# Revit family: ROSENBERG_KHAS
name_source: partatom
category: Wyposażenie mechaniczne
revit_build: Autodesk Revit 2017 (Build: 20160225_1515(x64)
units: mm (PartAtom-declared; Revit-internal decimal feet)

## family parameters
Numer OmniClass = 23.75.00.00
Oparty na płaszczyźnie roboczej = Nie
Punkt obliczania pomieszczeń = Nie
Tnij formami wycięć po wczytaniu = Nie
Typ części = Dzieli na
Tytuł OmniClass = Climate Control (HVAC)
Współdzielony = Tak
Wymiar okrągłego złącza = Użyj średnicy
Zawsze pionowo = Tak

## types (13) — shared parameters
2R = 250 mm  [stored 0.82021 ft]
Axis_fan = 40 mm  [stored 0.131234 ft]
Date = 10.2018
Frequency = 50 Hz
Insulation = 20 mm  [stored 0.0656168 ft]
Maintenance_space = Tak
Material = <Wg kategorii>
Opis = Duct Fan
Producent = Rosenberg
R = 320 mm  [stored 1.04987 ft]
URL = https://www.rosenberg.pl
Version = 1

## per-type parameters (varying)
| type | Air_flow | Current | Fan | Height | Height_connector | Hole | Length | Model | Power | Pressure | Protection Class | Voltage | Weight | Width | Width_connector |
| 500-4.6HF WS_400V | 5260.0 m³/h | 3 A | 554 mm | 500 mm  [stored 1.64042 ft] | 500 mm  [stored 1.64042 ft] | 800 mm  [stored 2.62467 ft] | 880 mm | 500-4.6HF WS | 1770 W | 540.0 Pa | IP54 | 400 V | 88.00 kg | 800 mm  [stored 2.62467 ft] | 800 mm  [stored 2.62467 ft] |
| 500-4.6HF WS | 4238.0 m³/h | 7 A | 554 mm | 500 mm  [stored 1.64042 ft] | 500 mm  [stored 1.64042 ft] | 170 mm  [stored 0.557743 ft] | 880 mm | 500-4.6HF WS | 1650 W | 540.0 Pa | IP54 | 230 V | 88.00 kg | 800 mm  [stored 2.62467 ft] | 800 mm  [stored 2.62467 ft] |
| 450-4.5HA WS_400V | 2927.0 m³/h | 2 A | 460 mm  [stored 1.50919 ft] | 400 mm  [stored 1.31234 ft] | 400 mm  [stored 1.31234 ft] | 170 mm  [stored 0.557743 ft] | 780 mm  [stored 2.55906 ft] | 450-4.5HA WS | 780 W | 427.0 Pa | IP54 | 400 V | 50.00 kg | 700 mm  [stored 2.29659 ft] | 700 mm  [stored 2.29659 ft] |
| 450-4.5HA WS | 2561.0 m³/h | 3 A | 440 mm | 400 mm  [stored 1.31234 ft] | 400 mm  [stored 1.31234 ft] | 170 mm  [stored 0.557743 ft] | 780 mm  [stored 2.55906 ft] | 450-4.5HA WS | 700 W | 388.0 Pa | IP54 | 230 V | 50.00 kg | 700 mm  [stored 2.29659 ft] | 700 mm  [stored 2.29659 ft] |
| 400-4.5DF WS_400V | 2205.0 m³/h | 1 A | 395 mm | 350 mm  [stored 1.14829 ft] | 350 mm  [stored 1.14829 ft] | 170 mm  [stored 0.557743 ft] | 700 mm  [stored 2.29659 ft] | 400-4.5DF WS | 500 W | 337.0 Pa | IP54 | 400 V | 36.00 kg | 600 mm | 600 mm |
| 400-4.5FA WS | 1805.0 m³/h | 3 A | 395 mm | 350 mm  [stored 1.14829 ft] | 350 mm  [stored 1.14829 ft] | 170 mm  [stored 0.557743 ft] | 700 mm  [stored 2.29659 ft] | 400-4.5FA WS | 540 W | 413.0 Pa | IP54 | 230 V | 38.00 kg | 600 mm | 600 mm |
| 355-4.4EC WS_400V | 1437.0 m³/h | 1 A | 390 mm | 350 mm  [stored 1.14829 ft] | 350 mm  [stored 1.14829 ft] | 170 mm  [stored 0.557743 ft] | 700 mm  [stored 2.29659 ft] | 355-4.4EC WS | 300 W | 282.0 Pa | IP54 | 400 V | 34.00 kg | 600 mm | 600 mm |
| 355-4.4FF WS | 1498.0 m³/h | 1 A | 390 mm | 350 mm  [stored 1.14829 ft] | 350 mm  [stored 1.14829 ft] | 170 mm  [stored 0.557743 ft] | 700 mm  [stored 2.29659 ft] | 355-4.4FF WS | 330 W | 290.0 Pa | IP54 | 230 V | 35.00 kg | 600 mm | 600 mm |
| 315-4.4DA WS_400V | 877.0 m³/h | 0 A | 272 mm | 250 mm  [stored 0.82021 ft] | 250 mm  [stored 0.82021 ft] | 170 mm  [stored 0.557743 ft] | 530 mm  [stored 1.73885 ft] | 315-4.4DA WS | 150 W | 206.0 Pa | IP54 | 400 V | 23.00 kg | 500 mm  [stored 1.64042 ft] | 500 mm  [stored 1.64042 ft] |
| 315-4.4DA WS | 921.0 m³/h | 1 A | 272 mm | 250 mm  [stored 0.82021 ft] | 250 mm  [stored 0.82021 ft] | 170 mm  [stored 0.557743 ft] | 530 mm  [stored 1.73885 ft] | 315-4.4DA WS | 167 W | 207.0 Pa | IP44 | 230 V | 23.00 kg | 500 mm  [stored 1.64042 ft] | 500 mm  [stored 1.64042 ft] |
| 280-2.5DF WS_400V | 1416.0 m³/h | 1 A | 272 mm | 250 mm  [stored 0.82021 ft] | 250 mm  [stored 0.82021 ft] | 170 mm  [stored 0.557743 ft] | 530 mm  [stored 1.73885 ft] | 280-2.5DF WS | 520 W | 557.0 Pa | IP54 | 400 V | 24.50 kg | 500 mm  [stored 1.64042 ft] | 500 mm  [stored 1.64042 ft] |
| 280-2.5DF WS | 1352.0 m³/h | 2 A | 272 mm | 250 mm  [stored 0.82021 ft] | 250 mm  [stored 0.82021 ft] | 170 mm  [stored 0.557743 ft] | 530 mm  [stored 1.73885 ft] | 280-2.5DF WS | 480 W | 484.0 Pa | IP54 | 230 V | 26.50 kg | 500 mm  [stored 1.64042 ft] | 500 mm  [stored 1.64042 ft] |
| 560-4.6LA RS | 6012.0 m³/h | 4 A | 554 mm | 500 mm  [stored 1.64042 ft] | 500 mm  [stored 1.64042 ft] | 800 mm  [stored 2.62467 ft] | 982 mm | 560-4.6LA RS | 2200 W | 646.0 Pa | IP54 | 400 V | 103.00 kg | 1000 mm  [stored 3.28084 ft] | 1000 mm  [stored 3.28084 ft] |

note: [stored X ft] marks values corroborated as IEEE doubles in the binary element streams (Revit-internal decimal feet)

## geometry (parser evidence)
native form markers: Blend x4, Sweep x5
no freeform markers — native parametric forms only
